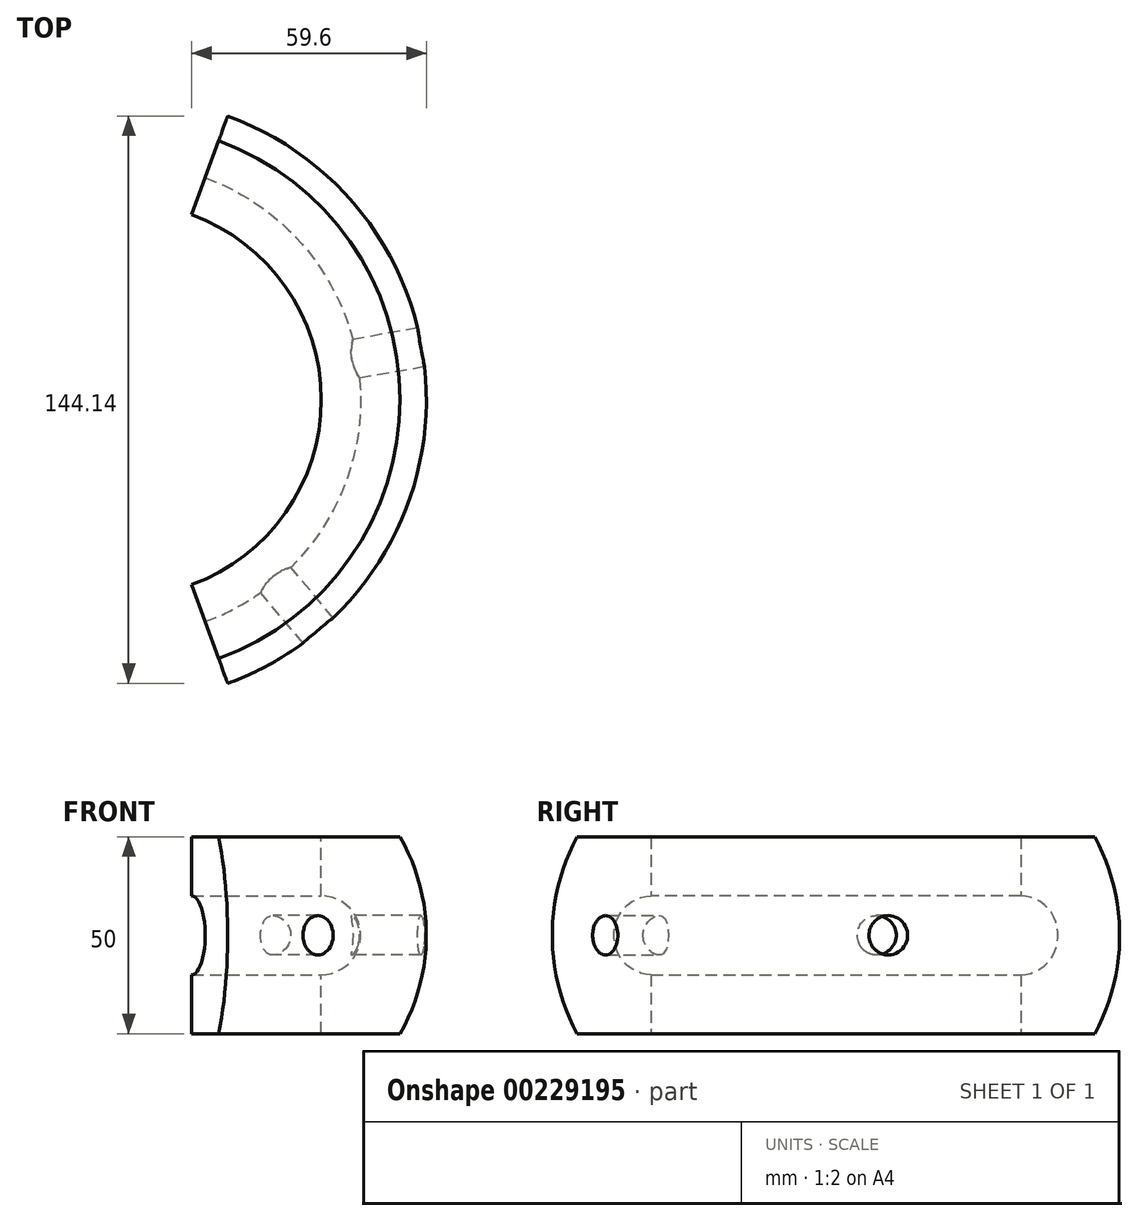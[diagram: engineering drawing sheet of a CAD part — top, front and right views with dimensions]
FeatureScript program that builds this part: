
annotation { "Feature Type Name" : "Feature", "Feature Type Description" : "" }
export const myFeature = defineFeature(function(context is Context, id is Id, definition is map)
    precondition{}
    {
        {
            var Q0;
            Q0=qCreatedBy(makeId("Front.planeOp"),FACE);
            var sketch = newSketch(context, id + "F0", { "sketchPlane" : qUnion([Q0])});
            skLineSegment(sketch, "E0", {"start": v(50, 25) * mm, "end": v(50, -25) * mm});
            skLineSegment(sketch, "E1", {"start": v(50, -25) * mm, "end": v(70, -25) * mm});
            skLineSegment(sketch, "E2", {"start": v(50, 25) * mm, "end": v(70, 25) * mm});
            skArc(sketch, "E3", {"start": v(70, -25) * mm, "mid": v(76.7, 0) * mm, "end": v(70, 25) * mm});
            skLineSegment(sketch, "E4", {"start": v(0, 66.75) * mm, "end": v(0, -48) * mm, "construction": true});
            skSolve(sketch);
        }
        {
            var Q0;
            Q0 = qSketchRegion(id + "F0", true);
            var Q1;
            Q1=sQuery(id+"F0.wireOp",EDGE,"E4");
            revolve(context, id + "F1", {"entities" : qUnion([Q0]), "axis" : qUnion([Q1]), "revolveType" : RevolveType.TWO_DIRECTIONS, "angle" : 70 * degree, "angleBack" : 290 * degree});
        }
        {
            var Q0;
            Q0=qCreatedBy(makeId("Front.planeOp"),FACE);
            var sketch = newSketch(context, id + "F2", { "sketchPlane" : qUnion([Q0])});
            skCircle(sketch, "E5", {"center": v(50, 0) * mm, "radius": 10 * mm});
            skSolve(sketch);
        }
        {
            var Q0;
            Q0 = qSketchRegion(id + "F2", true);
            var Q1;
            Q1=sQuery(id+"F0.wireOp",EDGE,"E4");
            revolve(context, id + "F3", {"operationType" : NewBodyOperationType.REMOVE, "entities" : qUnion([Q0]), "axis" : qUnion([Q1]), "revolveType" : RevolveType.FULL, "oppositeDirection" : true});
        }
        {
            var Q0;
            Q0=qCreatedBy(makeId("Top.planeOp"),FACE);
            var sketch = newSketch(context, id + "F4", { "sketchPlane" : qUnion([Q0])});
            skCircle(sketch, "E6", {"center": v(0, 0) * mm, "radius": 50 * mm, "construction": true});
            skLineSegment(sketch, "E7", {"start": v(0, 0) * mm, "end": v(19.16, 52.64) * mm, "construction": true});
            skCircle(sketch, "E8", {"center": v(17.1, 46.98) * mm, "radius": 50 * mm, "construction": true});
            skCircle(sketch, "E9", {"center": v(49.24, 8.68) * mm, "radius": 50 * mm, "construction": true});
            skLineSegment(sketch, "E10", {"start": v(0, 0) * mm, "end": v(49.24, 8.68) * mm, "construction": true});
            skLineSegment(sketch, "E11", {"start": v(0, 0) * mm, "end": v(32.14, -38.3) * mm, "construction": true});
            skSolve(sketch);
        }
        {
            var Q0;
            Q0=sQuery(id+"F4.wireOp",EDGE,"E10");
            var Q1;
            Q1=qCreatedBy(makeId("Origin.pointOp"),VERTEX);
            cPlane(context, id + "F5", {"entities" : qUnion([Q0, Q1]), "cplaneType" : CPlaneType.LINE_POINT, "offset" : 25 * mm, "width" : 150 * mm, "height" : 150 * mm});
        }
        {
            var Q0;
            Q0=qCreatedBy(id+"F5.planeOp",FACE);
            var sketch = newSketch(context, id + "F6", { "sketchPlane" : qUnion([Q0])});
            skCircle(sketch, "E12", {"center": v(0, 0) * mm, "radius": 5 * mm});
            skSolve(sketch);
        }
        {
            var Q0;
            Q0 = qSketchRegion(id + "F6", true);
            extrude(context, id + "F7", {"entities" : qUnion([Q0]), "operationType" : NewBodyOperationType.REMOVE, "endBound" : BoundingType.THROUGH_ALL, "depth" : 95.68 * mm});
        }
        {
            var Q0;
            Q0=sQuery(id+"F4.wireOp",EDGE,"E11");
            var Q1;
            Q1=qCreatedBy(makeId("Origin.pointOp"),VERTEX);
            cPlane(context, id + "F8", {"entities" : qUnion([Q0, Q1]), "cplaneType" : CPlaneType.LINE_POINT, "offset" : 25 * mm, "width" : 150 * mm, "height" : 150 * mm});
        }
        {
            var Q0;
            Q0=qCreatedBy(id+"F8.planeOp",FACE);
            var sketch = newSketch(context, id + "F9", { "sketchPlane" : qUnion([Q0])});
            skCircle(sketch, "E13", {"center": v(0, 0) * mm, "radius": 5 * mm});
            skSolve(sketch);
        }
        {
            var Q0;
            Q0 = qSketchRegion(id + "F9", true);
            extrude(context, id + "F10", {"entities" : qUnion([Q0]), "operationType" : NewBodyOperationType.REMOVE, "endBound" : BoundingType.THROUGH_ALL, "depth" : 25 * mm});
        }
    });
